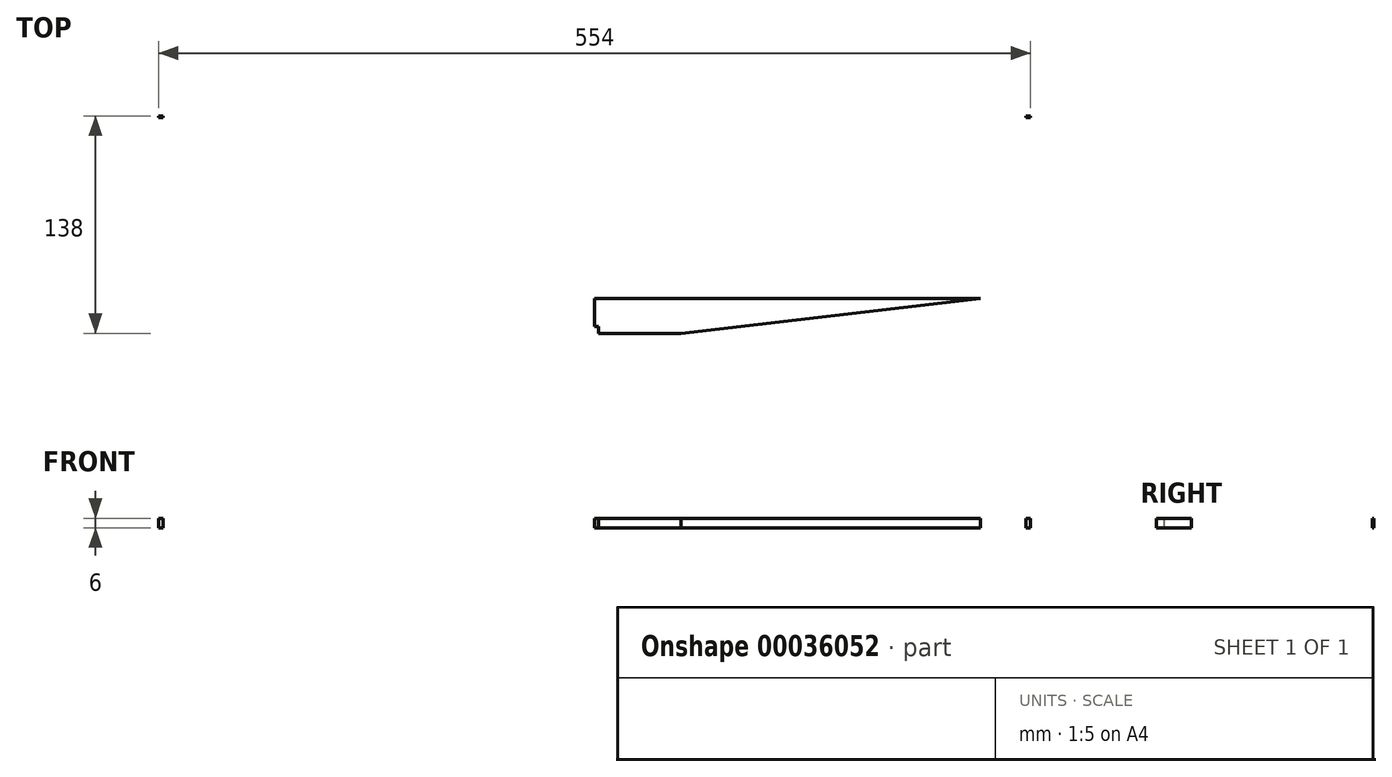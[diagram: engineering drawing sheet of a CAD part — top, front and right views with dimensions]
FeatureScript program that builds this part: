
annotation { "Feature Type Name" : "Feature", "Feature Type Description" : "" }
export const myFeature = defineFeature(function(context is Context, id is Id, definition is map)
    precondition{}
    {
        {
            var Q0;
            Q0=qCreatedBy(makeId("Top.planeOp"),FACE);
            var sketch = newSketch(context, id + "F0", { "sketchPlane" : qUnion([Q0])});
            skLineSegment(sketch, "E0.rect.bottom", {"start": v(-138.5, 115) * mm, "end": v(138.5, 115) * mm});
            skLineSegment(sketch, "E0.rect.top", {"start": v(-138.5, -115) * mm, "end": v(138.5, -115) * mm});
            skLineSegment(sketch, "E0.rect.left", {"start": v(-138.5, 115) * mm, "end": v(-138.5, -115) * mm});
            skPoint(sketch, "E0.rect.middle", {"position": v(0, 0) * mm});
            skLineSegment(sketch, "E1", {"start": v(-138.5, 115) * mm, "end": v(-108.5, 115) * mm});
            skLineSegment(sketch, "E2", {"start": v(-138.5, 115) * mm, "end": v(-136, 115) * mm});
            skLineSegment(sketch, "E3", {"start": v(-136, 115) * mm, "end": v(-136, 110.5) * mm});
            skLineSegment(sketch, "E4", {"start": v(-136, 110.5) * mm, "end": v(-138.5, 110.5) * mm});
            skLineSegment(sketch, "E5", {"start": v(-108.5, 115) * mm, "end": v(-108.5, 22) * mm});
            skLineSegment(sketch, "E6", {"start": v(-108.5, 22) * mm, "end": v(138.5, 22) * mm});
            skLineSegment(sketch, "E7", {"start": v(138.5, 22) * mm, "end": v(138.5, 89) * mm});
            skLineSegment(sketch, "E8", {"start": v(-108.5, 115) * mm, "end": v(138.5, 89) * mm});
            skLineSegment(sketch, "E9", {"start": v(-108.5, 22) * mm, "end": v(-107.5, 22) * mm});
            skLineSegment(sketch, "E10", {"start": v(-107.5, 22) * mm, "end": v(-107.5, 115) * mm});
            skLineSegment(sketch, "E11", {"start": v(138.5, 22) * mm, "end": v(138.5, 23) * mm});
            skLineSegment(sketch, "E12", {"start": v(138.5, 23) * mm, "end": v(135.5, 23) * mm});
            skLineSegment(sketch, "E13", {"start": v(135.5, 23) * mm, "end": v(135.5, 22) * mm});
            skLineSegment(sketch, "E14", {"start": v(-138.5, -93) * mm, "end": v(106.5, -93) * mm});
            skLineSegment(sketch, "E15", {"start": v(106.5, -93) * mm, "end": v(106.5, -115) * mm});
            skLineSegment(sketch, "E16", {"start": v(138.5, -115) * mm, "end": v(138.5, -55) * mm});
            skArc(sketch, "E17", {"start": v(106.5, -93) * mm, "mid": v(129.43, -79.84) * mm, "end": v(138.5, -55) * mm});
            skLineSegment(sketch, "E18", {"start": v(-138.5, -115) * mm, "end": v(-83.5, -115) * mm});
            skLineSegment(sketch, "E19", {"start": v(-83.5, -115) * mm, "end": v(106.5, -93) * mm});
            skLineSegment(sketch, "E20", {"start": v(138.5, -55) * mm, "end": v(138.5, 22) * mm});
            skLineSegment(sketch, "E21.bottom", {"start": v(-138.5, -115) * mm, "end": v(-136, -115) * mm});
            skLineSegment(sketch, "E21.top", {"start": v(-138.5, -110.5) * mm, "end": v(-136, -110.5) * mm});
            skLineSegment(sketch, "E21.left", {"start": v(-138.5, -115) * mm, "end": v(-138.5, -110.5) * mm});
            skLineSegment(sketch, "E21.right", {"start": v(-136, -115) * mm, "end": v(-136, -110.5) * mm});
            skSolve(sketch);
        }
        {
            var Q0;
            Q0=makeQuery(id+"F0.imprint","IMPRINT",FACE,{"disambiguationData":[TD([[makeQuery(id+"F0.imprint","IMPRINT",EDGE,{"derivedFrom":sQuery(id+"F0.wireOp",EDGE,"E1")}),-1.0]])]});
            var Q1;
            {var subQ6=sQuery(id+"F0.wireOp",EDGE,"E7");Q1=makeQuery(id+"F0.imprint","IMPRINT",FACE,{"disambiguationData":[TD([[makeQuery(id+"F0.imprint","IMPRINT",EDGE,{"derivedFrom":subQ6}),1.0]])]});}
            var Q2;
            {var subQ1=sQuery(id+"F0.wireOp",EDGE,"E14");Q2=makeQuery(id+"F0.imprint","IMPRINT",FACE,{"disambiguationData":[TD([[makeQuery(id+"F0.imprint","IMPRINT",EDGE,{"derivedFrom":subQ1}),-1.0]])]});}
            extrude(context, id + "F1", {"entities" : qUnion([Q0, Q1, Q2]), "depth" : 6 * mm});
        }
        {
            var Q0;
            Q0=makeQuery(id+"F1.opExtrude","SWEPT_FACE",FACE,{"disambiguationData":[OSD([sQuery(id+"F0.wireOp",EDGE,"E0.rect.left")])]});
            var sketch = newSketch(context, id + "F2", { "sketchPlane" : qUnion([Q0])});
            skLineSegment(sketch, "E22", {"start": v(110.5, 3) * mm, "end": v(-110.5, 3) * mm});
            skSolve(sketch);
        }
        {
            var Q0;
            Q0=makeQuery(id+"F1.opExtrude","SWEPT_BODY",BODY,{"disambiguationData":[OSD([sQuery(id+"F0.wireOp",EDGE,"E0.rect.left"),sQuery(id+"F0.wireOp",EDGE,"E1"),sQuery(id+"F0.wireOp",EDGE,"E3"),sQuery(id+"F0.wireOp",EDGE,"E4"),sQuery(id+"F0.wireOp",EDGE,"E5"),sQuery(id+"F0.wireOp",EDGE,"E6"),sQuery(id+"F0.wireOp",EDGE,"E7"),sQuery(id+"F0.wireOp",EDGE,"E8"),sQuery(id+"F0.wireOp",EDGE,"E9"),sQuery(id+"F0.wireOp",EDGE,"E10"),sQuery(id+"F0.wireOp",EDGE,"E12"),sQuery(id+"F0.wireOp",EDGE,"E13"),sQuery(id+"F0.wireOp",EDGE,"E17"),sQuery(id+"F0.wireOp",EDGE,"E18"),sQuery(id+"F0.wireOp",EDGE,"E19"),sQuery(id+"F0.wireOp",EDGE,"E20"),sQuery(id+"F0.wireOp",EDGE,"E21.top"),sQuery(id+"F0.wireOp",EDGE,"E21.right")])]});
            var Q1;
            Q1=sQuery(id+"F2.wireOp",EDGE,"E22");
            circularPattern(context, id + "F3", {"operationType" : NewBodyOperationType.ADD, "entities" : qUnion([Q0]), "axis" : qUnion([Q1]), "angle" : 180 * degree, "instanceCount" : 2});
        }
    });
